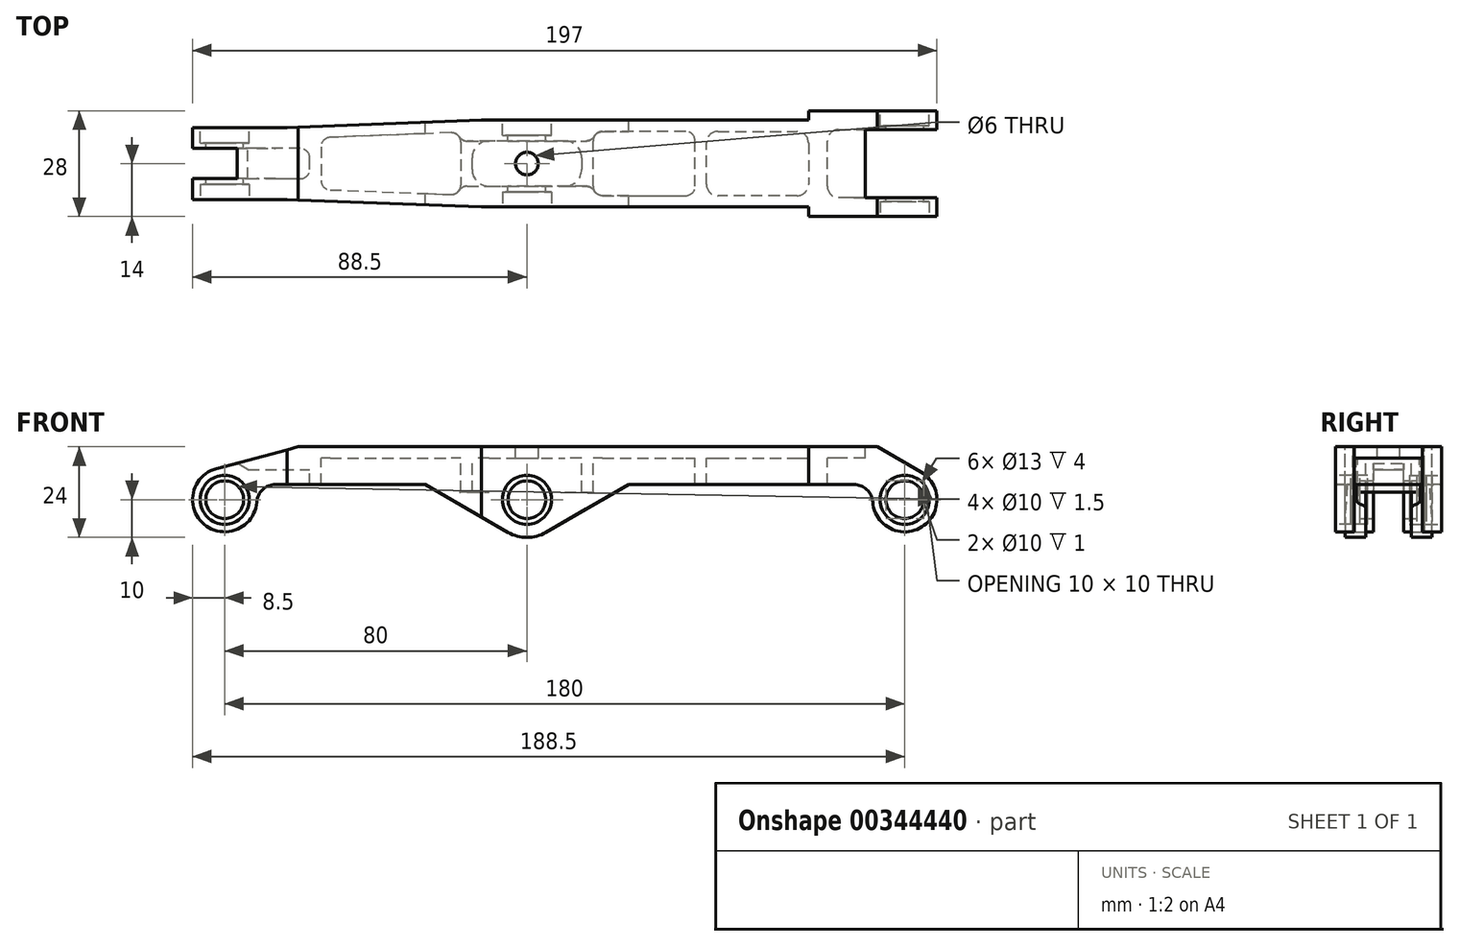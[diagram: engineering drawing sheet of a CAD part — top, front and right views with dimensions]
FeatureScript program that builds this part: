
annotation { "Feature Type Name" : "Feature", "Feature Type Description" : "" }
export const myFeature = defineFeature(function(context is Context, id is Id, definition is map)
    precondition{}
    {
        {
            var Q0;
            Q0=qCreatedBy(makeId("Front.planeOp"),FACE);
            var sketch = newSketch(context, id + "F0", { "sketchPlane" : qUnion([Q0])});
            skLineSegment(sketch, "E0", {"start": v(-60.6, 14) * mm, "end": v(92.75, 14) * mm});
            skArc(sketch, "E1", {"start": v(-82.2, 8.21) * mm, "mid": v(-85.42, -6.55) * mm, "end": v(-71.52, -0.63) * mm});
            skArc(sketch, "E2", {"start": v(91.52, -0.63) * mm, "mid": v(104.52, -7.2) * mm, "end": v(104.25, 7.36) * mm});
            skLineSegment(sketch, "E3", {"start": v(92.75, 14) * mm, "end": v(104.25, 7.36) * mm});
            skLineSegment(sketch, "E4", {"start": v(-60.6, 14) * mm, "end": v(-82.2, 8.21) * mm});
            skLineSegment(sketch, "E5", {"start": v(-66.54, 4) * mm, "end": v(-26.93, 4) * mm});
            skCircle(sketch, "E6", {"center": v(-80, 0) * mm, "radius": 5 * mm});
            skCircle(sketch, "E7", {"center": v(0, 0) * mm, "radius": 5 * mm});
            skCircle(sketch, "E8", {"center": v(100, 0) * mm, "radius": 5 * mm});
            skArc(sketch, "E9", {"start": v(-5, -8.66) * mm, "mid": v(0, -10) * mm, "end": v(5, -8.66) * mm});
            skLineSegment(sketch, "E10", {"start": v(26.93, 4) * mm, "end": v(5, -8.66) * mm});
            skLineSegment(sketch, "E11", {"start": v(-26.93, 4) * mm, "end": v(-5, -8.66) * mm});
            skLineSegment(sketch, "E12.trimOffspring", {"start": v(26.93, 4) * mm, "end": v(86.54, 4) * mm});
            skPoint(sketch, "E13.visualSharp", {"position": v(-72.5, 4) * mm});
            skArc(sketch, "E13.filletArc", {"start": v(-66.54, 4) * mm, "mid": v(-69.94, 2.66) * mm, "end": v(-71.52, -0.63) * mm});
            skPoint(sketch, "E14.visualSharp", {"position": v(92.5, 4) * mm});
            skArc(sketch, "E14.filletArc", {"start": v(91.52, -0.63) * mm, "mid": v(89.94, 2.66) * mm, "end": v(86.54, 4) * mm});
            skSolve(sketch);
        }
        {
            var Q0;
            Q0=makeQuery(id+"F0.imprint","IMPRINT",FACE,{"disambiguationData":[TD([[makeQuery(id+"F0.imprint","IMPRINT",EDGE,{"derivedFrom":sQuery(id+"F0.wireOp",EDGE,"E0")}),-1.0]])]});
            extrude(context, id + "F1", {"entities" : qUnion([Q0]), "endBound" : BoundingType.SYMMETRIC, "depth" : 28 * mm});
        }
        {
            var Q0;
            Q0=makeQuery(id+"F1.opExtrude","SWEPT_FACE",FACE,{"disambiguationData":[OSD([sQuery(id+"F0.wireOp",EDGE,"E0")])]});
            var sketch = newSketch(context, id + "F2", { "sketchPlane" : qUnion([Q0])});
            skLineSegment(sketch, "E15", {"start": v(-88.5, -9.5) * mm, "end": v(-63.5, -9.5) * mm});
            skLineSegment(sketch, "E16", {"start": v(-63.5, -9.5) * mm, "end": v(-12, -11.5) * mm});
            skLineSegment(sketch, "E17", {"start": v(-12, -11.5) * mm, "end": v(74.5, -11.5) * mm});
            skLineSegment(sketch, "E18", {"start": v(74.5, -11.5) * mm, "end": v(74.5, -14) * mm});
            skLineSegment(sketch, "E19", {"start": v(74.5, -14) * mm, "end": v(108.5, -14) * mm});
            skLineSegment(sketch, "E20", {"start": v(108.5, -9) * mm, "end": v(89.5, -9) * mm});
            skLineSegment(sketch, "E21", {"start": v(89.5, -9) * mm, "end": v(89.5, 9) * mm});
            skLineSegment(sketch, "E22", {"start": v(89.5, 9) * mm, "end": v(108.5, 9) * mm});
            skLineSegment(sketch, "E23", {"start": v(108.5, 9) * mm, "end": v(108.5, 14) * mm});
            skLineSegment(sketch, "E24", {"start": v(108.5, 14) * mm, "end": v(74.5, 14) * mm});
            skLineSegment(sketch, "E25", {"start": v(74.5, 14) * mm, "end": v(74.5, 11.5) * mm});
            skLineSegment(sketch, "E26", {"start": v(74.5, 11.5) * mm, "end": v(-12, 11.5) * mm});
            skLineSegment(sketch, "E27", {"start": v(-12, 11.5) * mm, "end": v(-63.5, 9.5) * mm});
            skLineSegment(sketch, "E28", {"start": v(-63.5, 9.5) * mm, "end": v(-88.5, 9.5) * mm});
            skLineSegment(sketch, "E29", {"start": v(108.5, 14) * mm, "end": v(108.5, 9) * mm});
            skLineSegment(sketch, "E30", {"start": v(108.5, -9) * mm, "end": v(108.5, -14) * mm});
            skLineSegment(sketch, "E31", {"start": v(-88.5, -9.5) * mm, "end": v(-88.5, 9.5) * mm});
            skLineSegment(sketch, "E32", {"start": v(-100, -25) * mm, "end": v(-100, 25) * mm});
            skLineSegment(sketch, "E33", {"start": v(-100, 25) * mm, "end": v(120, 25) * mm});
            skLineSegment(sketch, "E34", {"start": v(120, 25) * mm, "end": v(120, -25) * mm});
            skLineSegment(sketch, "E35", {"start": v(120, -25) * mm, "end": v(-100, -25) * mm});
            skPoint(sketch, "E36", {"position": v(0, 0) * mm});
            skSolve(sketch);
        }
        {
            var Q0;
            Q0 = qSketchRegion(id + "F2", true);
            extrude(context, id + "F3", {"entities" : qUnion([Q0]), "operationType" : NewBodyOperationType.REMOVE, "oppositeDirection" : true, "depth" : 25 * mm});
        }
        {
            var Q0;
            Q0=makeQuery(id+"F1.opExtrude","SWEPT_FACE",FACE,{"disambiguationData":[OSD([sQuery(id+"F0.wireOp",EDGE,"E12.trimOffspring")])]});
            var sketch = newSketch(context, id + "F4", { "sketchPlane" : qUnion([Q0])});
            skLineSegment(sketch, "E37", {"start": v(71.5, 8.5) * mm, "end": v(50.5, 8.5) * mm});
            skLineSegment(sketch, "E38", {"start": v(47.5, 5.5) * mm, "end": v(47.5, -5.5) * mm});
            skLineSegment(sketch, "E39", {"start": v(50.5, -8.5) * mm, "end": v(71.5, -8.5) * mm});
            skLineSegment(sketch, "E40", {"start": v(74.5, -5.5) * mm, "end": v(74.5, 5.5) * mm});
            skLineSegment(sketch, "E41", {"start": v(44.5, 6) * mm, "end": v(44.5, -6) * mm});
            skLineSegment(sketch, "E42", {"start": v(42, -8.5) * mm, "end": v(20, -8.5) * mm});
            skLineSegment(sketch, "E43", {"start": v(17.5, -6) * mm, "end": v(17.5, 6) * mm});
            skLineSegment(sketch, "E44", {"start": v(20, 8.5) * mm, "end": v(42, 8.5) * mm});
            skPoint(sketch, "E45.0", {"position": v(89.5, 9) * mm});
            skPoint(sketch, "E46.0", {"position": v(89.5, -9) * mm});
            skLineSegment(sketch, "E47", {"start": v(89.5, 9) * mm, "end": v(82.5, 9) * mm});
            skLineSegment(sketch, "E48", {"start": v(79.5, 6) * mm, "end": v(79.5, -6) * mm});
            skLineSegment(sketch, "E49", {"start": v(82.5, -9) * mm, "end": v(89.5, -9) * mm});
            skLineSegment(sketch, "E50", {"start": v(89.5, 9) * mm, "end": v(89.5, -9) * mm});
            skLineSegment(sketch, "E51", {"start": v(-17.5, 5.69) * mm, "end": v(-17.5, -5.69) * mm});
            skLineSegment(sketch, "E52", {"start": v(-20.1, -8.18) * mm, "end": v(-52.1, -6.94) * mm});
            skLineSegment(sketch, "E53", {"start": v(-54.5, -4.44) * mm, "end": v(-54.5, 4.44) * mm});
            skLineSegment(sketch, "E54", {"start": v(-52.1, 6.94) * mm, "end": v(-20.1, 8.18) * mm});
            skLineSegment(sketch, "E55", {"start": v(-14.5, -1.5) * mm, "end": v(-14.5, 1.5) * mm});
            skLineSegment(sketch, "E56", {"start": v(-10, 6) * mm, "end": v(10, 6) * mm});
            skLineSegment(sketch, "E57", {"start": v(14.5, 1.5) * mm, "end": v(14.5, -1.5) * mm});
            skLineSegment(sketch, "E58", {"start": v(10, -6) * mm, "end": v(-10, -6) * mm});
            skLineSegment(sketch, "E59", {"start": v(108.5, 14) * mm, "end": v(108.5, 9) * mm});
            skLineSegment(sketch, "E60", {"start": v(0, -20.2) * mm, "end": v(0, 23.55) * mm, "construction": true});
            skPoint(sketch, "E61.visualSharp", {"position": v(-54.5, 6.85) * mm});
            skArc(sketch, "E61.filletArc", {"start": v(-52.1, 6.94) * mm, "mid": v(-53.8, 6.18) * mm, "end": v(-54.5, 4.44) * mm});
            skPoint(sketch, "E62.visualSharp", {"position": v(-54.5, -6.85) * mm});
            skArc(sketch, "E62.filletArc", {"start": v(-54.5, -4.44) * mm, "mid": v(-53.8, -6.18) * mm, "end": v(-52.1, -6.94) * mm});
            skPoint(sketch, "E63.visualSharp", {"position": v(-17.5, 8.28) * mm});
            skArc(sketch, "E63.filletArc", {"start": v(-17.5, 5.69) * mm, "mid": v(-18.27, 7.49) * mm, "end": v(-20.1, 8.18) * mm});
            skPoint(sketch, "E64.visualSharp", {"position": v(-17.5, -8.28) * mm});
            skArc(sketch, "E64.filletArc", {"start": v(-20.1, -8.18) * mm, "mid": v(-18.27, -7.49) * mm, "end": v(-17.5, -5.69) * mm});
            skPoint(sketch, "E65.visualSharp", {"position": v(-14.5, 6) * mm});
            skArc(sketch, "E65.filletArc", {"start": v(-10, 6) * mm, "mid": v(-13.18, 4.68) * mm, "end": v(-14.5, 1.5) * mm});
            skPoint(sketch, "E66.visualSharp", {"position": v(14.5, 6) * mm});
            skArc(sketch, "E66.filletArc", {"start": v(14.5, 1.5) * mm, "mid": v(13.18, 4.68) * mm, "end": v(10, 6) * mm});
            skPoint(sketch, "E67.visualSharp", {"position": v(14.5, -6) * mm});
            skArc(sketch, "E67.filletArc", {"start": v(10, -6) * mm, "mid": v(13.18, -4.68) * mm, "end": v(14.5, -1.5) * mm});
            skPoint(sketch, "E68.visualSharp", {"position": v(-14.5, -6) * mm});
            skArc(sketch, "E68.filletArc", {"start": v(-14.5, -1.5) * mm, "mid": v(-13.18, -4.68) * mm, "end": v(-10, -6) * mm});
            skPoint(sketch, "E69.visualSharp", {"position": v(79.5, 9) * mm});
            skArc(sketch, "E69.filletArc", {"start": v(82.5, 9) * mm, "mid": v(80.38, 8.12) * mm, "end": v(79.5, 6) * mm});
            skPoint(sketch, "E70.visualSharp", {"position": v(79.5, -9) * mm});
            skArc(sketch, "E70.filletArc", {"start": v(79.5, -6) * mm, "mid": v(80.38, -8.12) * mm, "end": v(82.5, -9) * mm});
            skPoint(sketch, "E71.visualSharp", {"position": v(47.5, 8.5) * mm});
            skArc(sketch, "E71.filletArc", {"start": v(50.5, 8.5) * mm, "mid": v(48.38, 7.62) * mm, "end": v(47.5, 5.5) * mm});
            skPoint(sketch, "E72.visualSharp", {"position": v(47.5, -8.5) * mm});
            skArc(sketch, "E72.filletArc", {"start": v(47.5, -5.5) * mm, "mid": v(48.38, -7.62) * mm, "end": v(50.5, -8.5) * mm});
            skPoint(sketch, "E73.visualSharp", {"position": v(74.5, -8.5) * mm});
            skArc(sketch, "E73.filletArc", {"start": v(71.5, -8.5) * mm, "mid": v(73.62, -7.62) * mm, "end": v(74.5, -5.5) * mm});
            skPoint(sketch, "E74.visualSharp", {"position": v(74.5, 8.5) * mm});
            skArc(sketch, "E74.filletArc", {"start": v(74.5, 5.5) * mm, "mid": v(73.62, 7.62) * mm, "end": v(71.5, 8.5) * mm});
            skPoint(sketch, "E75.visualSharp", {"position": v(17.5, 8.5) * mm});
            skArc(sketch, "E75.filletArc", {"start": v(20, 8.5) * mm, "mid": v(18.23, 7.77) * mm, "end": v(17.5, 6) * mm});
            skPoint(sketch, "E76.visualSharp", {"position": v(17.5, -8.5) * mm});
            skArc(sketch, "E76.filletArc", {"start": v(17.5, -6) * mm, "mid": v(18.23, -7.77) * mm, "end": v(20, -8.5) * mm});
            skPoint(sketch, "E77.visualSharp", {"position": v(44.5, -8.5) * mm});
            skArc(sketch, "E77.filletArc", {"start": v(42, -8.5) * mm, "mid": v(43.77, -7.77) * mm, "end": v(44.5, -6) * mm});
            skPoint(sketch, "E78.visualSharp", {"position": v(44.5, 8.5) * mm});
            skArc(sketch, "E78.filletArc", {"start": v(44.5, 6) * mm, "mid": v(43.77, 7.77) * mm, "end": v(42, 8.5) * mm});
            skSolve(sketch);
        }
        {
            var Q0;
            Q0 = qSketchRegion(id + "F4", true);
            extrude(context, id + "F5", {"entities" : qUnion([Q0]), "operationType" : NewBodyOperationType.REMOVE, "depth" : 25 * mm, "hasSecondDirection" : true, "secondDirectionOppositeDirection" : true, "secondDirectionDepth" : 7 * mm});
        }
        {
            var Q0;
            Q0=makeQuery(id+"F1.opExtrude","SWEPT_FACE",FACE,{"disambiguationData":[OSD([sQuery(id+"F0.wireOp",EDGE,"E5")])]});
            var sketch = newSketch(context, id + "F6", { "sketchPlane" : qUnion([Q0])});
            skLineSegment(sketch, "E79", {"start": v(-88.5, -4) * mm, "end": v(-88.5, 4) * mm});
            skLineSegment(sketch, "E80", {"start": v(-88.5, 4) * mm, "end": v(-60, 4) * mm});
            skLineSegment(sketch, "E81", {"start": v(-57.5, 1.5) * mm, "end": v(-57.5, -1.5) * mm});
            skLineSegment(sketch, "E82", {"start": v(-60, -4) * mm, "end": v(-88.5, -4) * mm});
            skPoint(sketch, "E83.visualSharp", {"position": v(-57.5, 4) * mm});
            skArc(sketch, "E83.filletArc", {"start": v(-57.5, 1.5) * mm, "mid": v(-58.23, 3.27) * mm, "end": v(-60, 4) * mm});
            skPoint(sketch, "E84.visualSharp", {"position": v(-57.5, -4) * mm});
            skArc(sketch, "E84.filletArc", {"start": v(-60, -4) * mm, "mid": v(-58.23, -3.27) * mm, "end": v(-57.5, -1.5) * mm});
            skSolve(sketch);
        }
        {
            var Q0;
            Q0 = qSketchRegion(id + "F6", true);
            extrude(context, id + "F7", {"entities" : qUnion([Q0]), "operationType" : NewBodyOperationType.REMOVE, "depth" : 25 * mm, "hasSecondDirection" : true, "secondDirectionOppositeDirection" : true, "secondDirectionDepth" : 4 * mm});
        }
        {
            var Q0;
            Q0=qCreatedBy(makeId("Front.planeOp"),FACE);
            var sketch = newSketch(context, id + "F8", { "sketchPlane" : qUnion([Q0])});
            skLineSegment(sketch, "E85", {"start": v(-86.07, 15.05) * mm, "end": v(-62.9, 1.67) * mm});
            skCircle(sketch, "E86.0", {"center": v(-80, 0) * mm, "radius": 5 * mm});
            skLineSegment(sketch, "E87", {"start": v(-86.07, 15.05) * mm, "end": v(-90.88, 6.73) * mm});
            skLineSegment(sketch, "E88", {"start": v(-90.88, 6.73) * mm, "end": v(-67.94, -6.5) * mm});
            skLineSegment(sketch, "E89", {"start": v(-67.94, -6.5) * mm, "end": v(-62.9, 1.67) * mm});
            skSolve(sketch);
        }
        {
            var Q0;
            Q0 = qSketchRegion(id + "F8", true);
            var Q1;
            Q1=makeQuery(id+"F7.boolean.opBoolean","COPY",FACE,{"derivedFrom":makeQuery(id+"F7.opExtrude","SWEPT_FACE",FACE,{"disambiguationData":[OSD([sQuery(id+"F6.wireOp",EDGE,"E82")])]})});
            var Q2;
            Q2=makeQuery(id+"F7.boolean.opBoolean","COPY",FACE,{"derivedFrom":makeQuery(id+"F7.opExtrude","SWEPT_FACE",FACE,{"disambiguationData":[OSD([sQuery(id+"F6.wireOp",EDGE,"E80")])]})});
            extrude(context, id + "F9", {"entities" : qUnion([Q0]), "operationType" : NewBodyOperationType.REMOVE, "endBound" : BoundingType.UP_TO_SURFACE, "oppositeDirection" : true, "endBoundEntityFace" : qUnion([Q1]), "depth" : 25 * mm, "hasSecondDirection" : true, "secondDirectionBound" : SecondDirectionBoundingType.UP_TO_SURFACE, "secondDirectionOppositeDirection" : false, "secondDirectionBoundEntityFace" : qUnion([Q2]), "secondDirectionDepth" : 25 * mm});
        }
        {
            var Q0;
            Q0=qCreatedBy(makeId("Top.planeOp"),FACE);
            cPlane(context, id + "F10", {"entities" : qUnion([Q0]), "cplaneType" : CPlaneType.OFFSET, "offset" : 10 * mm, "oppositeDirection" : true, "width" : 150 * mm, "height" : 150 * mm});
        }
        {
            var Q0;
            Q0=qCreatedBy(id+"F10.planeOp",FACE);
            var sketch = newSketch(context, id + "F11", { "sketchPlane" : qUnion([Q0])});
            skLineSegment(sketch, "E90.0.2", {"start": v(10, -6) * mm, "end": v(-10, -6) * mm});
            skLineSegment(sketch, "E90.0.6", {"start": v(-10, 6) * mm, "end": v(10, 6) * mm});
            skLineSegment(sketch, "E91", {"start": v(-10, -6) * mm, "end": v(-20.41, -6) * mm});
            skLineSegment(sketch, "E92", {"start": v(10, -6) * mm, "end": v(20.68, -6) * mm});
            skLineSegment(sketch, "E93", {"start": v(10, 6) * mm, "end": v(20.4, 6) * mm});
            skLineSegment(sketch, "E94", {"start": v(20.68, -6) * mm, "end": v(20.4, 6) * mm});
            skLineSegment(sketch, "E95", {"start": v(-10, 6) * mm, "end": v(-21.25, 6) * mm});
            skLineSegment(sketch, "E96", {"start": v(-21.25, 6) * mm, "end": v(-20.41, -6) * mm});
            skSolve(sketch);
        }
        {
            var Q0;
            Q0 = qSketchRegion(id + "F11", true);
            extrude(context, id + "F12", {"entities" : qUnion([Q0]), "operationType" : NewBodyOperationType.REMOVE, "depth" : 12 * mm});
        }
        {
            var Q0;
            Q0=makeQuery(id+"F12.boolean.opBoolean","INTERSECT",EDGE,{"derivedFrom":[makeQuery(id+"F5.boolean.opBoolean","COPY",FACE,{"derivedFrom":makeQuery(id+"F5.opExtrude","SWEPT_FACE",FACE,{"disambiguationData":[OSD([sQuery(id+"F4.wireOp",EDGE,"E63.filletArc")])]})}),makeQuery(id+"F12.opExtrude","SWEPT_FACE",FACE,{"disambiguationData":[OSD([sQuery(id+"F11.wireOp",EDGE,"E90.0.2"),sQuery(id+"F11.wireOp",EDGE,"E91"),sQuery(id+"F11.wireOp",EDGE,"E92")])]})]});
            var Q1;
            {var subQ0=sQuery(id+"F4.wireOp",EDGE,"E75.filletArc");Q1=makeQuery(id+"F12.boolean.opBoolean","SPLIT",EDGE,{"disambiguationData":[topologyDisambiguationEdgeConnected([makeQuery(id+"F5.boolean.opBoolean","COPY",FACE,{"derivedFrom":makeQuery(id+"F5.opExtrude","SWEPT_FACE",FACE,{"disambiguationData":[OSD([sQuery(id+"F4.wireOp",EDGE,"E56")])]})})])],"derivedFrom":makeQuery(id+"F5.boolean.opBoolean","COPY",EDGE,{"derivedFrom":makeQuery(id+"F5.opExtrude","SWEPT_EDGE",EDGE,{"disambiguationData":[OSD([sQuery(id+"F4.wireOp",EDGE,"E43"),subQ0])]})})});}
            var Q2;
            Q2=makeQuery(id+"F12.boolean.opBoolean","INTERSECT",EDGE,{"derivedFrom":[makeQuery(id+"F5.boolean.opBoolean","COPY",FACE,{"derivedFrom":makeQuery(id+"F5.opExtrude","SWEPT_FACE",FACE,{"disambiguationData":[OSD([sQuery(id+"F4.wireOp",EDGE,"E64.filletArc")])]})}),makeQuery(id+"F12.opExtrude","SWEPT_FACE",FACE,{"disambiguationData":[OSD([sQuery(id+"F11.wireOp",EDGE,"E90.0.6"),sQuery(id+"F11.wireOp",EDGE,"E93"),sQuery(id+"F11.wireOp",EDGE,"E95")])]})]});
            var Q3;
            {var subQ0=sQuery(id+"F4.wireOp",EDGE,"E76.filletArc");Q3=makeQuery(id+"F12.boolean.opBoolean","SPLIT",EDGE,{"disambiguationData":[topologyDisambiguationEdgeConnected([makeQuery(id+"F5.boolean.opBoolean","COPY",FACE,{"derivedFrom":makeQuery(id+"F5.opExtrude","SWEPT_FACE",FACE,{"disambiguationData":[OSD([sQuery(id+"F4.wireOp",EDGE,"E58")])]})})])],"derivedFrom":makeQuery(id+"F5.boolean.opBoolean","COPY",EDGE,{"derivedFrom":makeQuery(id+"F5.opExtrude","SWEPT_EDGE",EDGE,{"disambiguationData":[OSD([sQuery(id+"F4.wireOp",EDGE,"E43"),subQ0])]})})});}
            fillet(context, id + "F13", {"entities" : qUnion([Q0, Q1, Q2, Q3]), "radius" : 2.5 * mm, "tangentPropagation" : true, "allowEdgeOverflow" : false});
        }
        {
            var Q0;
            Q0=sQuery(id+"F2.wireOp",VERTEX,"E36");
            var Q1;
            Q1=makeQuery(id+"F1.opExtrude","SWEPT_BODY",BODY,{"disambiguationData":[OSD([sQuery(id+"F0.wireOp",EDGE,"E0"),sQuery(id+"F0.wireOp",EDGE,"E1"),sQuery(id+"F0.wireOp",EDGE,"E2"),sQuery(id+"F0.wireOp",EDGE,"E3"),sQuery(id+"F0.wireOp",EDGE,"E4"),sQuery(id+"F0.wireOp",EDGE,"E5"),sQuery(id+"F0.wireOp",EDGE,"E6"),sQuery(id+"F0.wireOp",EDGE,"E7"),sQuery(id+"F0.wireOp",EDGE,"E8"),sQuery(id+"F0.wireOp",EDGE,"E9"),sQuery(id+"F0.wireOp",EDGE,"E10"),sQuery(id+"F0.wireOp",EDGE,"E11"),sQuery(id+"F0.wireOp",EDGE,"E12.trimOffspring"),sQuery(id+"F0.wireOp",EDGE,"E13.filletArc"),sQuery(id+"F0.wireOp",EDGE,"E14.filletArc")])]});
            hole(context, id + "F14", {"style" : HoleStyle.SIMPLE, "endStyle" : HoleEndStyle.THROUGH, "holeDiameter" : 6 * mm, "isTappedThrough" : true, "tappedDepth" : 12 * mm, "tapClearance" : 3, "locations" : qUnion([Q0]), "scope" : qUnion([Q1])});
        }
        {
            var Q0;
            Q0=makeQuery(id+"F3.boolean.opBoolean","COPY",FACE,{"derivedFrom":makeQuery(id+"F3.opExtrude","SWEPT_FACE",FACE,{"disambiguationData":[OSD([sQuery(id+"F2.wireOp",EDGE,"E15")])]})});
            var sketch = newSketch(context, id + "F15", { "sketchPlane" : qUnion([Q0])});
            skPoint(sketch, "E97.0", {"position": v(-80, 0) * mm});
            skSolve(sketch);
        }
        {
            var Q0;
            Q0=makeQuery(id+"F3.boolean.opBoolean","COPY",FACE,{"derivedFrom":makeQuery(id+"F3.opExtrude","SWEPT_FACE",FACE,{"disambiguationData":[OSD([sQuery(id+"F2.wireOp",EDGE,"E17")])]})});
            var sketch = newSketch(context, id + "F16", { "sketchPlane" : qUnion([Q0])});
            skPoint(sketch, "E98.0", {"position": v(0, 0) * mm});
            skSolve(sketch);
        }
        {
            var Q0;
            Q0=makeQuery(id+"F1.opExtrude","CAP_FACE",FACE,{"disambiguationData":[OSD([sQuery(id+"F0.wireOp",EDGE,"E0"),sQuery(id+"F0.wireOp",EDGE,"E1"),sQuery(id+"F0.wireOp",EDGE,"E2"),sQuery(id+"F0.wireOp",EDGE,"E3"),sQuery(id+"F0.wireOp",EDGE,"E4"),sQuery(id+"F0.wireOp",EDGE,"E5"),sQuery(id+"F0.wireOp",EDGE,"E6"),sQuery(id+"F0.wireOp",EDGE,"E7"),sQuery(id+"F0.wireOp",EDGE,"E8"),sQuery(id+"F0.wireOp",EDGE,"E9"),sQuery(id+"F0.wireOp",EDGE,"E10"),sQuery(id+"F0.wireOp",EDGE,"E11"),sQuery(id+"F0.wireOp",EDGE,"E12.trimOffspring"),sQuery(id+"F0.wireOp",EDGE,"E13.filletArc"),sQuery(id+"F0.wireOp",EDGE,"E14.filletArc")])],"isStart":false});
            var sketch = newSketch(context, id + "F17", { "sketchPlane" : qUnion([Q0])});
            skPoint(sketch, "E99", {"position": v(100, 0) * mm});
            skSolve(sketch);
        }
        {
            var Q0;
            Q0=sQuery(id+"F15.wireOp",VERTEX,"E97.0");
            var Q1;
            Q1=sQuery(id+"F16.wireOp",VERTEX,"E98.0");
            var Q2;
            Q2=sQuery(id+"F17.wireOp",VERTEX,"E99");
            var Q3;
            Q3=makeQuery(id+"F1.opExtrude","SWEPT_BODY",BODY,{"disambiguationData":[OSD([sQuery(id+"F0.wireOp",EDGE,"E0"),sQuery(id+"F0.wireOp",EDGE,"E1"),sQuery(id+"F0.wireOp",EDGE,"E2"),sQuery(id+"F0.wireOp",EDGE,"E3"),sQuery(id+"F0.wireOp",EDGE,"E4"),sQuery(id+"F0.wireOp",EDGE,"E5"),sQuery(id+"F0.wireOp",EDGE,"E6"),sQuery(id+"F0.wireOp",EDGE,"E7"),sQuery(id+"F0.wireOp",EDGE,"E8"),sQuery(id+"F0.wireOp",EDGE,"E9"),sQuery(id+"F0.wireOp",EDGE,"E10"),sQuery(id+"F0.wireOp",EDGE,"E11"),sQuery(id+"F0.wireOp",EDGE,"E12.trimOffspring"),sQuery(id+"F0.wireOp",EDGE,"E13.filletArc"),sQuery(id+"F0.wireOp",EDGE,"E14.filletArc")])]});
            hole(context, id + "F18", {"style" : HoleStyle.C_BORE, "endStyle" : HoleEndStyle.BLIND, "holeDiameter" : 1 * mm, "cBoreDiameter" : 13 * mm, "cBoreDepth" : 4 * mm, "holeDepth" : 12 * mm, "isTappedThrough" : true, "tappedDepth" : 12 * mm, "tapClearance" : 3, "locations" : qUnion([Q0, Q1, Q2]), "scope" : qUnion([Q3])});
        }
        {
            var Q0;
            Q0=makeQuery(id+"F1.opExtrude","CAP_FACE",FACE,{"disambiguationData":[OSD([sQuery(id+"F0.wireOp",EDGE,"E0"),sQuery(id+"F0.wireOp",EDGE,"E1"),sQuery(id+"F0.wireOp",EDGE,"E2"),sQuery(id+"F0.wireOp",EDGE,"E3"),sQuery(id+"F0.wireOp",EDGE,"E4"),sQuery(id+"F0.wireOp",EDGE,"E5"),sQuery(id+"F0.wireOp",EDGE,"E6"),sQuery(id+"F0.wireOp",EDGE,"E7"),sQuery(id+"F0.wireOp",EDGE,"E8"),sQuery(id+"F0.wireOp",EDGE,"E9"),sQuery(id+"F0.wireOp",EDGE,"E10"),sQuery(id+"F0.wireOp",EDGE,"E11"),sQuery(id+"F0.wireOp",EDGE,"E12.trimOffspring"),sQuery(id+"F0.wireOp",EDGE,"E13.filletArc"),sQuery(id+"F0.wireOp",EDGE,"E14.filletArc")])],"isStart":true});
            var sketch = newSketch(context, id + "F19", { "sketchPlane" : qUnion([Q0])});
            skPoint(sketch, "E100.0", {"position": v(-100, 0) * mm});
            skSolve(sketch);
        }
        {
            var Q0;
            Q0=makeQuery(id+"F3.boolean.opBoolean","COPY",FACE,{"derivedFrom":makeQuery(id+"F3.opExtrude","SWEPT_FACE",FACE,{"disambiguationData":[OSD([sQuery(id+"F2.wireOp",EDGE,"E26")])]})});
            var sketch = newSketch(context, id + "F20", { "sketchPlane" : qUnion([Q0])});
            skPoint(sketch, "E101.0", {"position": v(0, 0) * mm});
            skSolve(sketch);
        }
        {
            var Q0;
            Q0=makeQuery(id+"F3.boolean.opBoolean","COPY",FACE,{"derivedFrom":makeQuery(id+"F3.opExtrude","SWEPT_FACE",FACE,{"disambiguationData":[OSD([sQuery(id+"F2.wireOp",EDGE,"E28")])]})});
            var sketch = newSketch(context, id + "F21", { "sketchPlane" : qUnion([Q0])});
            skPoint(sketch, "E102.0", {"position": v(80, 0) * mm});
            skSolve(sketch);
        }
        {
            var Q0;
            Q0=sQuery(id+"F19.wireOp",VERTEX,"E100.0");
            var Q1;
            Q1=sQuery(id+"F20.wireOp",VERTEX,"E101.0");
            var Q2;
            Q2=sQuery(id+"F21.wireOp",VERTEX,"E102.0");
            var Q3;
            Q3=makeQuery(id+"F1.opExtrude","SWEPT_BODY",BODY,{"disambiguationData":[OSD([sQuery(id+"F0.wireOp",EDGE,"E0"),sQuery(id+"F0.wireOp",EDGE,"E1"),sQuery(id+"F0.wireOp",EDGE,"E2"),sQuery(id+"F0.wireOp",EDGE,"E3"),sQuery(id+"F0.wireOp",EDGE,"E4"),sQuery(id+"F0.wireOp",EDGE,"E5"),sQuery(id+"F0.wireOp",EDGE,"E6"),sQuery(id+"F0.wireOp",EDGE,"E7"),sQuery(id+"F0.wireOp",EDGE,"E8"),sQuery(id+"F0.wireOp",EDGE,"E9"),sQuery(id+"F0.wireOp",EDGE,"E10"),sQuery(id+"F0.wireOp",EDGE,"E11"),sQuery(id+"F0.wireOp",EDGE,"E12.trimOffspring"),sQuery(id+"F0.wireOp",EDGE,"E13.filletArc"),sQuery(id+"F0.wireOp",EDGE,"E14.filletArc")])]});
            hole(context, id + "F22", {"style" : HoleStyle.C_BORE, "endStyle" : HoleEndStyle.BLIND, "holeDiameter" : 1 * mm, "cBoreDiameter" : 13 * mm, "cBoreDepth" : 4 * mm, "holeDepth" : 12 * mm, "isTappedThrough" : true, "tappedDepth" : 12 * mm, "tapClearance" : 3, "locations" : qUnion([Q0, Q1, Q2]), "scope" : qUnion([Q3])});
        }
    });
